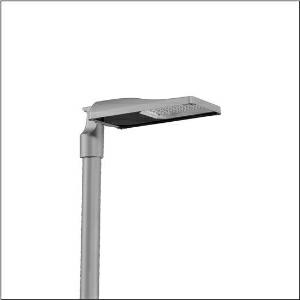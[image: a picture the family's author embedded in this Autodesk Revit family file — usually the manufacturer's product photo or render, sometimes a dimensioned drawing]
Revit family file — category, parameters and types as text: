
# Revit family: streetlight_sl_31_mini___p1_0a_5xh2a5aa08ha_a734
name_source: partatom
category: Lighting Fixtures
units: mm (PartAtom-declared; Revit-internal decimal feet)

## family parameters
Cut with Voids When Loaded = No
Host = Face
Light Source = No
Part Type = Normal
Room Calculation Point = No
Round Connector Dimension = Use Diameter
Shared = No

## types (1)
- --- (1 x LED, 7880 lm, 68.3 W, 3000K)
    Apparent Load = 68 VA
    CIE Flux Codes = 23 55 94 100 100
    Color Rendering = 80
    Color Temperature = 3000K
    Default Elevation = 1800 mm
    Description = Streetlight SL 31 mini Easy mast luminaire for post-top, side-entry; light control with lens of PMMA; light distribution: P1.0a, direct asymmetric distribution, for standard-compliant lighting for roads and squares; LED: luminous flux: 7.880lm, light colour: 830, colour temperature: 3000K; luminous efficacy: 115,4lm/W; control: overheat protection, intelligent temperature release in ECG and LED module, constant luminous flux control, time-dependent luminous flux control, flexible luminous flux parameterisation, pre-setting: linear dimming characteristic; luminaire housing, of diecast aluminium, Siteco® metallic grey (DB 702S), corrosivity category C5 high according to DIN EN ISO 12944; cover of toughened safety glass, transparent, mast flange of diecast aluminium, Siteco® metallic grey (DB 702S), spigot size: 76/60mm, mast flange included unmounted; with cable H07RN-F 2x 1.5mm², cable length: 8,5m, connection cable pre-assembled; mains connection: 220..240V, AC, 50/60Hz; power consumption (at start of service life): 68,3W / (at end of service life): 74,8W / (with reduced operation 50%): 29,4W; protection rating (complete): IP66; insulation class (complete): insulation class II (safety insulation); impact resistance: IK10; certification: CE, ENEC, ENEC+, VDE, UKCA; permissible operating ambient temperature for outdoor applications: -40..+50°C; packaging unit: 1 piece

Light Distribution: P1.0a
    Height = 76 mm
    Lamp = 1 x LED
    Lamp Light Flux = 7880 lm
    Lamp Power = 68.3 W
    Lamp count = 1
    Length = 547 mm
    Luminous efficacy = 115 lm/W
    Manufacturer = Siteco
    ModVariant = No
    Model = 5XH2A5AA08HA
    Number of Poles = 1
    OnlyDefault = Yes
    Power Factor = 1
    Product Name = Streetlight SL 31 mini | P1.0a
    Product group = mast luminaire | pylon top
    ProductGroupID = 6100
    Protection Class = Protection class II
    Protection Degree = IP 66
    RLX_Detail_Level = 1
    RLX_Emergency_Light_Flux = 0 lm
    RLX_Emergency_Type = 0
    RLX_Emergency_Type_DB = No
    RlxData = <blob elided: 39105 chars, md5=da33c800>
    Socket = socket
    Standby Power = 0 W
    System Light Flux = 7880 lm
    System Power = 68 W
    Type Comments = factory setting: luminous flux: 100 % | dim-lin: 254 | 693 mA
    Type Image = l_1300326.jpg
    URL = http://relux.com
    VarID = @adj_078415
    Voltage = 0 V
    Weight = 0.00 kg
    Width = 265 mm

## geometry (parser evidence)
native form markers: Blend x4, Sweep x8
no freeform markers — native parametric forms only
